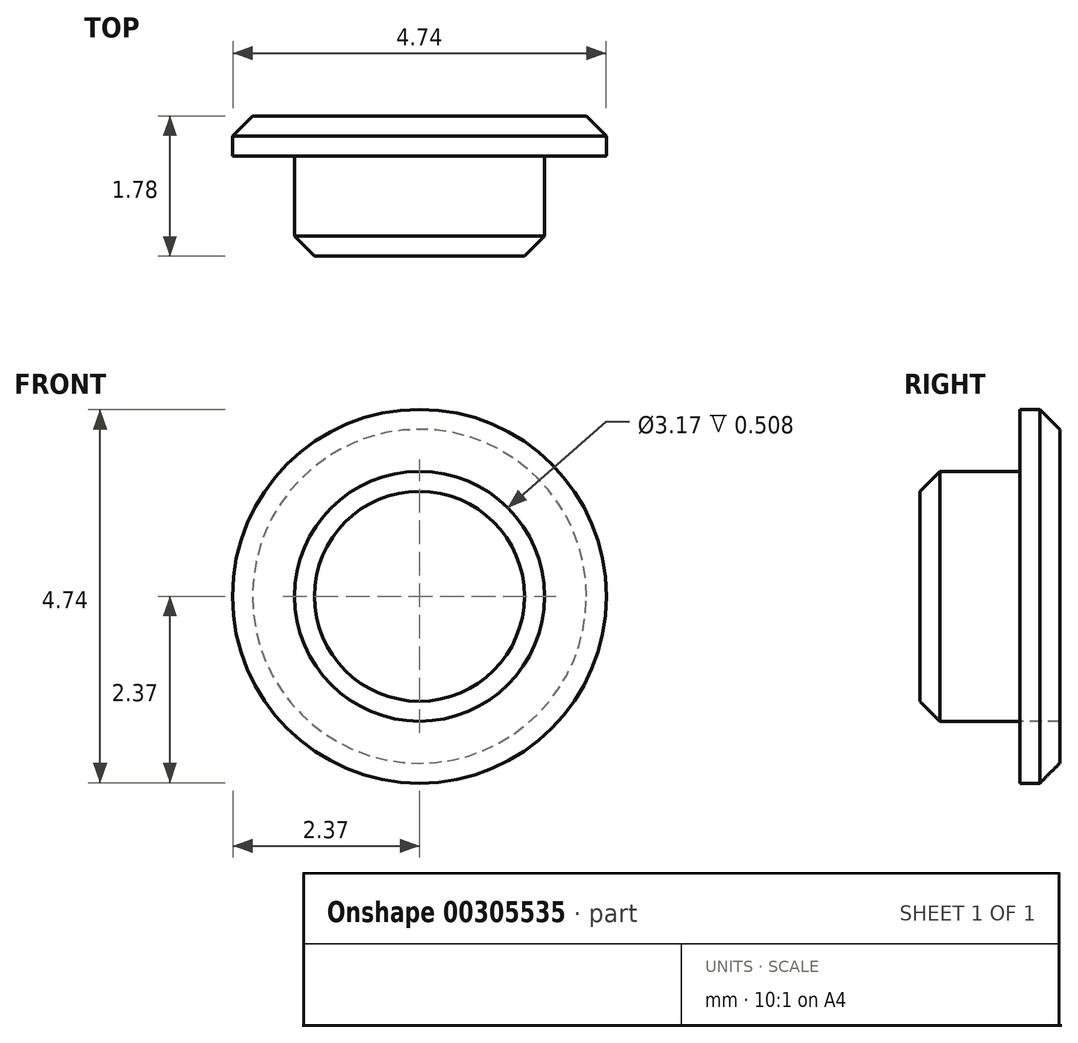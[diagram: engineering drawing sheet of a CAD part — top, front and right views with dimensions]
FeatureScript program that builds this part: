
annotation { "Feature Type Name" : "Feature", "Feature Type Description" : "" }
export const myFeature = defineFeature(function(context is Context, id is Id, definition is map)
    precondition{}
    {
        {
            var Q0;
            Q0=qCreatedBy(makeId("Front.planeOp"),FACE);
            var sketch = newSketch(context, id + "F0", { "sketchPlane" : qUnion([Q0])});
            skCircle(sketch, "E0", {"center": v(0, 0) * mm, "radius": 1.59 * mm});
            skCircle(sketch, "E1", {"center": v(0, 0) * mm, "radius": 2.37 * mm});
            skSolve(sketch);
        }
        {
            var Q0;
            Q0=makeQuery(id+"F0.imprint","IMPRINT",FACE,{"disambiguationData":[TD([[makeQuery(id+"F0.imprint","IMPRINT",EDGE,{"derivedFrom":sQuery(id+"F0.wireOp",EDGE,"E0")}),1.0]])]});
            extrude(context, id + "F1", {"entities" : qUnion([Q0]), "depth" : 1.27 * mm, "hasSecondDirection" : true, "secondDirectionOppositeDirection" : true, "secondDirectionDepth" : 0.5 * mm});
        }
        {
            var Q0;
            Q0=makeQuery(id+"F0.imprint","IMPRINT",FACE,{"disambiguationData":[TD([[makeQuery(id+"F0.imprint","IMPRINT",EDGE,{"derivedFrom":sQuery(id+"F0.wireOp",EDGE,"E0")}),-1.0]])]});
            extrude(context, id + "F2", {"entities" : qUnion([Q0]), "oppositeDirection" : true, "depth" : 0.5 * mm});
        }
        {
            var Q0;
            Q0=makeQuery(id+"F2.opExtrude","CAP_EDGE",EDGE,{"disambiguationData":[OSD([sQuery(id+"F0.wireOp",EDGE,"E1")])],"isStart":false});
            var Q1;
            Q1=makeQuery(id+"F1.opExtrude","CAP_EDGE",EDGE,{"disambiguationData":[OSD([sQuery(id+"F0.wireOp",EDGE,"E0")])],"isStart":false});
            chamfer(context, id + "F3", {"entities" : qUnion([Q0, Q1]), "width" : 0.25 * mm, "tangentPropagation" : true});
        }
    });
